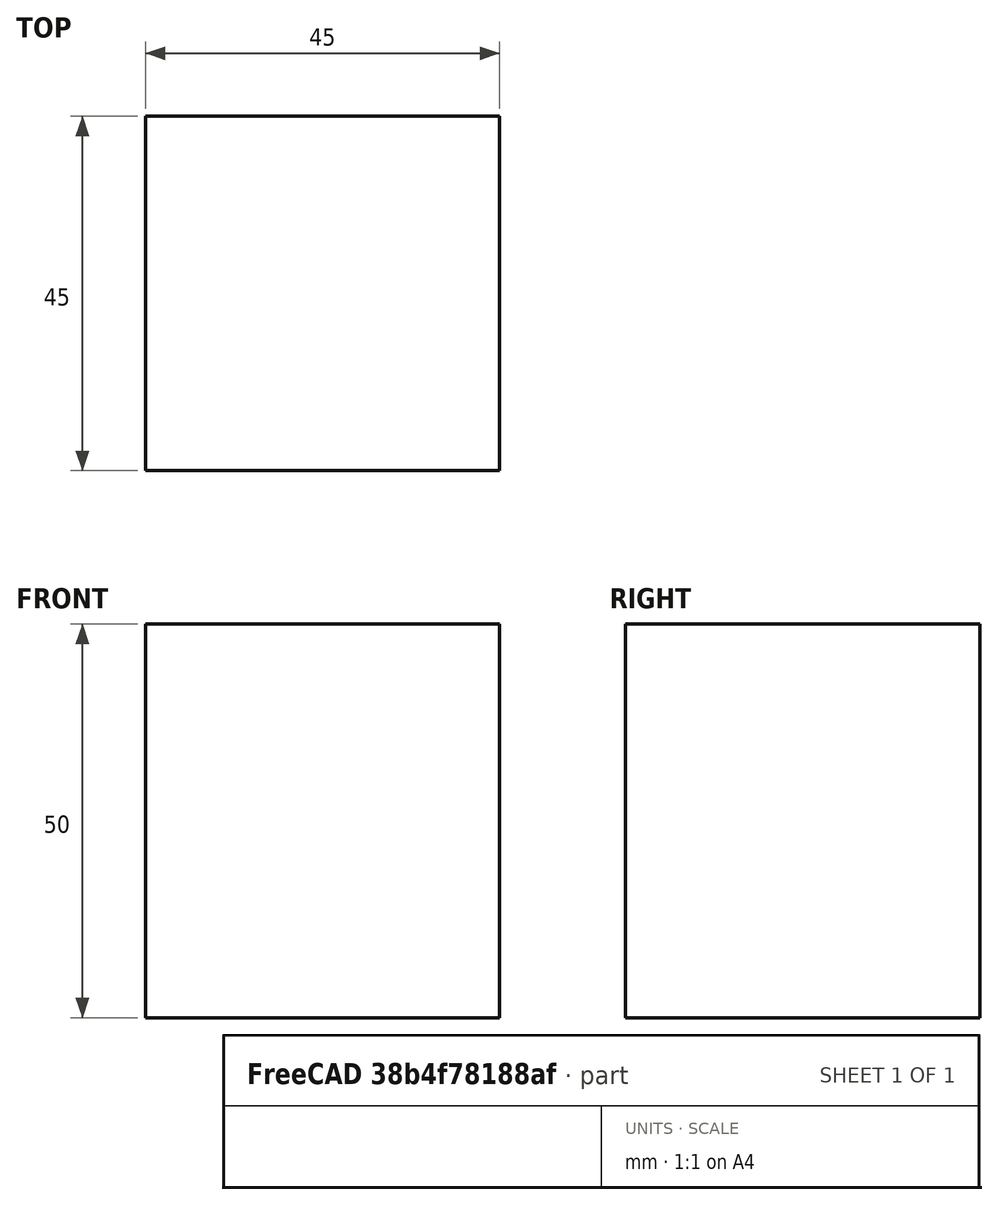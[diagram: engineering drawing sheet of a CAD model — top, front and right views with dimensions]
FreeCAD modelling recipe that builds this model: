
FCSTD DOCUMENT  (FreeCAD 0.15R4671 (Git))
Label: Square Bar 45 EN10059 S235JR
License: All rights reserved
LicenseURL: http://en.wikipedia.org/wiki/All_rights_reserved
objects: Sketcher::SketchObject×1, Part::Extrusion×1
note: 2 computed .brp shape members not serialized (recipe doc carries the construction recipe); baked Part::Feature solids carry a one-line shape summary decoded from their .brp

FEATURE [Sketcher::SketchObject] Sketch
  sketch-geometry (4):
    g0: LineSegment StartX=-22.5 StartY=-22.5 StartZ=0 EndX=22.5 EndY=-22.5 EndZ=0
    g1: LineSegment StartX=22.5 StartY=-22.5 StartZ=0 EndX=22.5 EndY=22.5 EndZ=0
    g2: LineSegment StartX=22.5 StartY=22.5 StartZ=0 EndX=-22.5 EndY=22.5 EndZ=0
    g3: LineSegment StartX=-22.5 StartY=22.5 StartZ=0 EndX=-22.5 EndY=-22.5 EndZ=0
  constraints (12):
    c: Coincident(g0,g1)
    c: Coincident(g1,g2)
    c: Coincident(g2,g3)
    c: Coincident(g3,g0)
    c: Horizontal(g0)
    c: Horizontal(g2)
    c: Vertical(g1)
    c: Vertical(g3)
    c: Symmetric(g1,g0,g-1)
    c: Symmetric(g2,g1,g-2)
    c: Equal(g1,g2)
    c: DistanceY(g1) = 45
FEATURE [Part::Extrusion] Extrude  label="Square Bar 45 EN10059 S235JR"
  Base = -> Sketch
  Dir = (0,0,50)
  Solid = true
